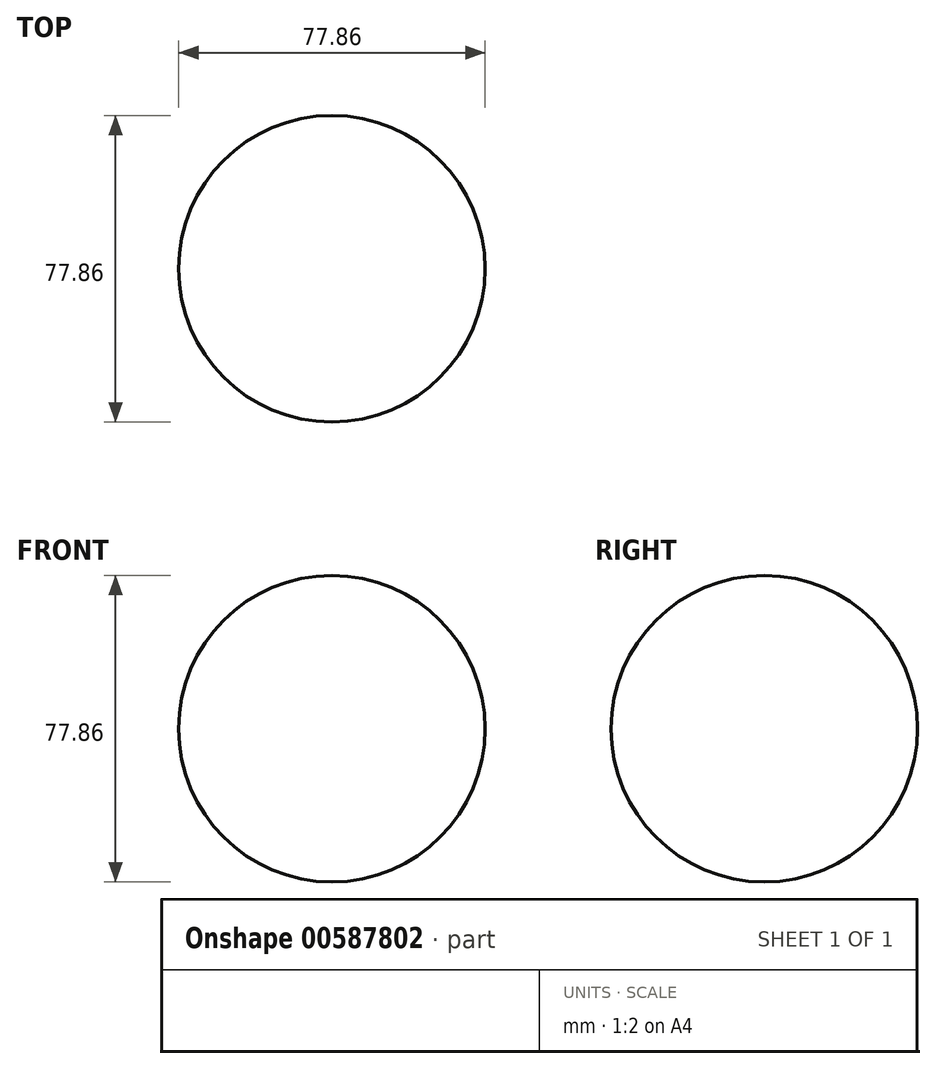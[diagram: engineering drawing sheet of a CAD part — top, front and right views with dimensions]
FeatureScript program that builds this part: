
annotation { "Feature Type Name" : "Feature", "Feature Type Description" : "" }
export const myFeature = defineFeature(function(context is Context, id is Id, definition is map)
    precondition{}
    {
        {
            var Q0;
            Q0=qCreatedBy(makeId("Front.planeOp"),FACE);
            var sketch = newSketch(context, id + "F0", { "sketchPlane" : qUnion([Q0])});
            skLineSegment(sketch, "E0", {"start": v(0, 71.8) * mm, "end": v(0, -46.92) * mm, "construction": true});
            skArc(sketch, "E1", {"start": v(0, 38.93) * mm, "mid": v(38.93, 0) * mm, "end": v(0, -38.93) * mm});
            skLineSegment(sketch, "E2", {"start": v(0, -38.93) * mm, "end": v(0, 38.93) * mm});
            skSolve(sketch);
        }
        {
            var Q0;
            Q0 = qSketchRegion(id + "F0", true);
            var Q1;
            Q1=sQuery(id+"F0.wireOp",EDGE,"E0");
            revolve(context, id + "F1", {"entities" : qUnion([Q0]), "axis" : qUnion([Q1]), "revolveType" : RevolveType.FULL});
        }
    });
